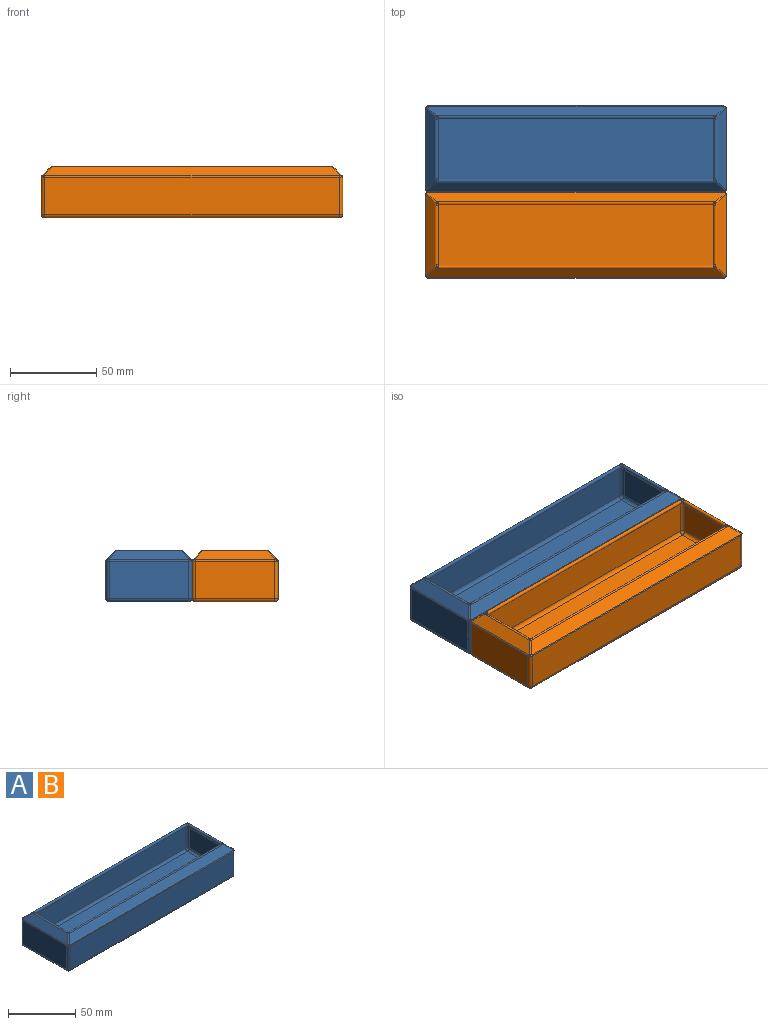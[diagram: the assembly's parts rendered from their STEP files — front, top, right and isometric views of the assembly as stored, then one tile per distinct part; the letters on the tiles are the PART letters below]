
ASSEMBLY  parts=2 mates=1
PART A: 84 faces, bbox 175x50x30 mm
  f0: plane 1.41x1.41mm, normal (0,0,1), area 0.4mm2, adj f62,f68,f69
  f1: plane 1.41x1.41mm, normal (0,0,1), area 0.4mm2, adj f56,f63,f69
  f2: plane 1.41x1.41mm, normal (0,0,1), area 0.4mm2, adj f51,f52,f56
  f3: plane 1.41x1.41mm, normal (0,0,1), area 0.4mm2, adj f52,f61,f68
  f4: plane 46x21.59mm, normal (-1,0,0), area 992.9mm2, adj f38,f44,f47,f59
  f5: plane 171x21.59mm, normal (0,-1,0), area 3691.2mm2, adj f36,f38,f39,f66
  f6: plane 46x21.59mm, normal (1,0,0), area 992.9mm2, adj f36,f40,f41,f81
  f7: plane 171x21.59mm, normal (0,1,0), area 3691.2mm2, adj f41,f45,f47,f77
  f8: plane 171x46mm, normal (0,0,-1), area 7866mm2, adj f39,f40,f44,f45
  f9: plane 47.41x5.41mm, normal (-0.71,0,0.71), area 325.8mm2, adj f49,f50,f56,f59,f64,f65
  f10: plane 172.41x5.41mm, normal (0,-0.71,0.71), area 1282.9mm2, adj f49,f52,f60,f66,f72,f73
  f11: plane 172.41x5.41mm, normal (0,0.71,0.71), area 1282.9mm2, adj f64,f69,f74,f77,f79,f80
  f12: plane 47.41x5.41mm, normal (0.71,0,0.71), area 325.8mm2, adj f68,f73,f78,f79,f81,f83
  f13: plane 42x18.34mm, normal (1,0,0), area 770.4mm2, adj f30,f33,f34,f35
  f14: plane 167x19.17mm, normal (0,1,0), area 3201.7mm2, adj f19,f23,f28,f33
  f15: plane 42x18.34mm, normal (-1,0,0), area 770.4mm2, adj f22,f23,f24,f25
  f16: plane 167x19.17mm, normal (0,-1,0), area 3201.7mm2, adj f20,f24,f29,f34
  f17: plane 167x42mm, normal (0,0,1), area 7014mm2, adj f25,f28,f29,f30
  f18: plane 43.41x4.54mm, normal (0.71,0,-0.71), area 249.4mm2, adj f35,f48,f55,f56
  f19: plane 169.03x5.12mm, normal (0,0.71,-0.71), area 1190.8mm2, adj f14,f23,f33,f48,f52,f53
  f20: plane 169.03x5.12mm, normal (0,-0.71,-0.71), area 1190.8mm2, adj f16,f24,f34,f54,f55,f69
  f21: plane 43.41x4.54mm, normal (-0.71,0,-0.71), area 249.4mm2, adj f22,f53,f54,f68
  f22: cylinder r=2mm len=44.37mm, axis (0,-1,0), area 68.1mm2, adj f15,f21,f23,f24,f53,f54
  f23: cylinder r=2mm len=19.57mm, axis (0,0,1), area 60.4mm2, adj f14,f15,f19,f22,f26,f53
  f24: cylinder r=2mm len=19.57mm, axis (0,0,-1), area 60.4mm2, adj f15,f16,f20,f22,f27,f54
  f25: cylinder r=2mm len=42mm, axis (0,-1,0), area 131.9mm2, adj f15,f17,f26,f27
  f26: sphere r=2mm, area 6.3mm2, adj f23,f25,f28
  f27: sphere r=2mm, area 6.3mm2, adj f24,f25,f29
  f28: cylinder r=2mm len=167mm, axis (-1,0,0), area 524.6mm2, adj f14,f17,f26,f31
  f29: cylinder r=2mm len=167mm, axis (1,0,0), area 524.6mm2, adj f16,f17,f27,f32
  f30: cylinder r=2mm len=42mm, axis (0,1,0), area 131.9mm2, adj f13,f17,f31,f32
  f31: sphere r=2mm, area 6.3mm2, adj f28,f30,f33
  f32: sphere r=2mm, area 6.3mm2, adj f29,f30,f34
  f33: cylinder r=2mm len=19.57mm, axis (0,0,-1), area 60.4mm2, adj f13,f14,f19,f31,f35,f48
  f34: cylinder r=2mm len=19.57mm, axis (0,0,1), area 60.4mm2, adj f13,f16,f20,f32,f35,f55
  f35: cylinder r=2mm len=44.37mm, axis (0,1,0), area 68.1mm2, adj f13,f18,f33,f34,f48,f55
  f36: cylinder r=2mm len=21.88mm, axis (0,0,-1), area 68.1mm2, adj f5,f6,f37,f72,f78
  f37: sphere r=2mm, area 6.3mm2, adj f36,f39,f40
  f38: cylinder r=2mm len=21.88mm, axis (0,0,1), area 68.1mm2, adj f4,f5,f42,f50,f60
  f39: cylinder r=2mm len=171mm, axis (1,0,0), area 537.2mm2, adj f5,f8,f37,f42
  f40: cylinder r=2mm len=46mm, axis (0,1,0), area 144.5mm2, adj f6,f8,f37,f43
  f41: cylinder r=2mm len=21.88mm, axis (0,0,1), area 68.1mm2, adj f6,f7,f43,f80,f83
  f42: sphere r=2mm, area 6.3mm2, adj f38,f39,f44
  f43: sphere r=2mm, area 6.3mm2, adj f40,f41,f45
  f44: cylinder r=2mm len=46mm, axis (0,-1,0), area 144.5mm2, adj f4,f8,f42,f46
  f45: cylinder r=2mm len=171mm, axis (-1,0,0), area 537.2mm2, adj f7,f8,f43,f46
  f46: sphere r=2mm, area 6.3mm2, adj f44,f45,f47
  f47: cylinder r=2mm len=21.88mm, axis (0,0,-1), area 68.1mm2, adj f4,f7,f46,f65,f74
  f48: cylinder r=1mm len=5.55mm, axis (-0.58,-0.58,-0.58), area 8.5mm2, adj f18,f19,f33,f35,f51
  f49: cylinder r=1mm len=5.83mm, axis (0.58,0.58,0.58), area 9.3mm2, adj f9,f10,f57,f58
  f50: bspline ~1.41x1mm, area 1.1mm2, adj f9,f38,f57,f59
  f51: bspline ~1.82x1.41mm, area 2.8mm2, adj f2,f48,f52,f56
  f52: cylinder r=1mm len=162.17mm, axis (-1,0,0), area 502.8mm2, adj f2,f3,f10,f19,f51,f58,f61,f67
  f53: cylinder r=1mm len=5.55mm, axis (-0.58,0.58,0.58), area 8.5mm2, adj f19,f21,f22,f23,f61
  f54: cylinder r=1mm len=5.55mm, axis (-0.58,-0.58,0.58), area 8.5mm2, adj f20,f21,f22,f24,f62
  f55: cylinder r=1mm len=5.55mm, axis (-0.58,0.58,-0.58), area 8.5mm2, adj f18,f20,f34,f35,f63
  f56: cylinder r=1mm len=37.17mm, axis (0,-1,0), area 110.1mm2, adj f1,f2,f9,f18,f51,f58,f63,f70
  f57: sphere r=1mm, area 0.6mm2, adj f49,f50,f60
  f58: sphere r=1mm, area 0.3mm2, adj f49,f52,f56
  f59: cylinder r=1mm len=46mm, axis (0,-1,0), area 36.1mm2, adj f4,f9,f50,f65
  f60: bspline ~1.41x1mm, area 1.1mm2, adj f10,f38,f57,f66
  f61: bspline ~1.82x1.41mm, area 2.8mm2, adj f3,f52,f53,f68
  f62: bspline ~1.82x1.41mm, area 2.8mm2, adj f0,f54,f68,f69
  f63: bspline ~1.82x1.41mm, area 2.8mm2, adj f1,f55,f56,f69
  f64: cylinder r=1mm len=5.83mm, axis (0.58,-0.58,0.58), area 9.3mm2, adj f9,f11,f70,f71
  f65: bspline ~1.41x1mm, area 1.1mm2, adj f9,f47,f59,f71
  f66: cylinder r=1mm len=171mm, axis (1,0,0), area 134.3mm2, adj f5,f10,f60,f72
  f67: sphere r=1mm, area 0.3mm2, adj f52,f68,f73
  f68: cylinder r=1mm len=37.17mm, axis (0,-1,0), area 110.1mm2, adj f0,f3,f12,f21,f61,f62,f67,f76
  f69: cylinder r=1mm len=162.17mm, axis (-1,0,0), area 502.8mm2, adj f0,f1,f11,f20,f62,f63,f70,f76
  f70: sphere r=1mm, area 0.3mm2, adj f56,f64,f69
  f71: sphere r=1mm, area 0.6mm2, adj f64,f65,f74
  f72: bspline ~1.41x1mm, area 1.1mm2, adj f10,f36,f66,f75
  f73: cylinder r=1mm len=5.83mm, axis (0.58,-0.58,-0.58), area 9.3mm2, adj f10,f12,f67,f75
  f74: bspline ~1.41x1mm, area 1.1mm2, adj f11,f47,f71,f77
  f75: sphere r=1mm, area 0.6mm2, adj f72,f73,f78
  f76: sphere r=1mm, area 0.3mm2, adj f68,f69,f79
  f77: cylinder r=1mm len=171mm, axis (-1,0,0), area 134.3mm2, adj f7,f11,f74,f80
  f78: bspline ~1.41x1mm, area 1.1mm2, adj f12,f36,f75,f81
  f79: cylinder r=1mm len=5.83mm, axis (0.58,0.58,-0.58), area 9.3mm2, adj f11,f12,f76,f82
  f80: bspline ~1.41x1mm, area 1.1mm2, adj f11,f41,f77,f82
  f81: cylinder r=1mm len=46mm, axis (0,1,0), area 36.1mm2, adj f6,f12,f78,f83
  f82: sphere r=1mm, area 0.6mm2, adj f79,f80,f83
  f83: bspline ~1.41x1mm, area 1.1mm2, adj f12,f41,f81,f82
PART B: same geometry as A
PLACE A t=(-30.39,8.8,-49.95)mm
PLACE B t=(-30.39,-41.2,-49.95)mm
MATE parallel A.f5 <-> B.f7  axis (0,-1,0) through (19.03,8.8,-37.16)mm
